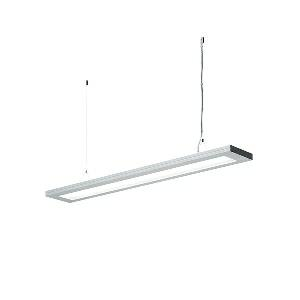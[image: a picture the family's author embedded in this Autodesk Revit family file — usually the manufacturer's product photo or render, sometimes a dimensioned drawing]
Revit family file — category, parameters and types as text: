
# Revit family: lavigo_-_dpp_9000_840_r_g2_00800468_b6bb
name_source: partatom
category: Lighting Fixtures
units: mm (PartAtom-declared; Revit-internal decimal feet)

## family parameters
Cut with Voids When Loaded = No
Host = Face
Light Source = No
Part Type = Normal
Room Calculation Point = No
Round Connector Dimension = Use Diameter
Shared = No

## types (1)
- LAVIGO - DPP 9000/840/R/G2 (1 x LED, 9350 lm, 4000K)
    Apparent Load = 65 VA
    Approval mark = CE
    CIE Flux Codes = 60 87 97 19 100
    Color Rendering = 80-89
    Color Temperature = 4000K
    Control Gear = Electronic ballast
    Default Elevation = 1800 mm
    Description = DPP 9000/840/R/G2|Suspended luminaire|light source: LED|connected load: 220-240V, 50/60Hz|Power consumption: approx. 65 W|standby: approx. 0,50|luminous flux: 9350 lm|luminous efficacy: 143 lm/W|light distribution: Direct/indirect|direct ratio: approx. 19 %|colour temperature: Cold white, ca. 4000 K|color rendering index (CRI): >= 80|chromaticity tolerance:  3 SDCM|System of protection: IP 20|technology: Presence and daylight sensor control (PIR)|luminaire body|material: Steel/plastic|surface: Powder coatet|colour: White|lamp cover: Polycarbonate (PC), Clear|mains lead: 1.00 m With free stranded wires|Fastening: Steel cable 0.3 - 0.7 m|decorative contrast side parts: Flint grey|glare control: Prism aperture|luminance(L65): <= 2800 cd/m|unified glare rating(4H 8H): <=  16|special features: Canopy colour (pure white), Push button in luminaire head, Cradle to Cradle Certified TM, Direct light component with edge light and light-guide technology for homogenous light exit, Integrated light and presence sensor PIR, Retrofittable with TALK module, Separated, direct and indirect light individually adjustable|
    Frequency = 50 Hz
    Height = 36 mm
    Lamp = 1 x LED
    Lamp Light Flux = 9350 lm
    Lamp count = 1
    Length = 1245 mm
    Luminous efficacy = 144 lm/W
    Manufacturer = Waldmann
    ModVariant = No
    Model = 00800468
    Mounting Place = Ceiling
    Mounting Type = Pendant
    Number of Poles = 1
    OnlyDefault = Yes
    Power Factor = 1
    Product Name = LAVIGO - DPP 9000/840/R/G2
    Product group = Suspended luminaire
    ProductGroupID = 9
    Protection Class = Protection class I
    Protection Degree = IP 20
    RLX_Detail_Level = 1
    RLX_Emergency_Light_Flux = 0 lm
    RLX_Emergency_Type = 0
    RLX_Emergency_Type_DB = No
    RlxData = <blob elided: 24305 chars, md5=3e5861dc>
    Socket = socket
    Standby Power = 0 W
    System Light Flux = 9350 lm
    System Power = 65 W
    Type Comments = Product without accessories
    Type Image = 121740000-00678744.jpg
    URL = http://relux.com
    VarID = ---
    Voltage = 230 V
    Voltage Range = 220-240 V
    Weight = 0.00 kg
    Width = 200 mm  [stored 0.656168 ft]

note: [stored X ft] marks values corroborated as IEEE doubles in the binary element streams (Revit-internal decimal feet)

## geometry (parser evidence)
native form markers: Blend x4, Sweep x14
no freeform markers — native parametric forms only
